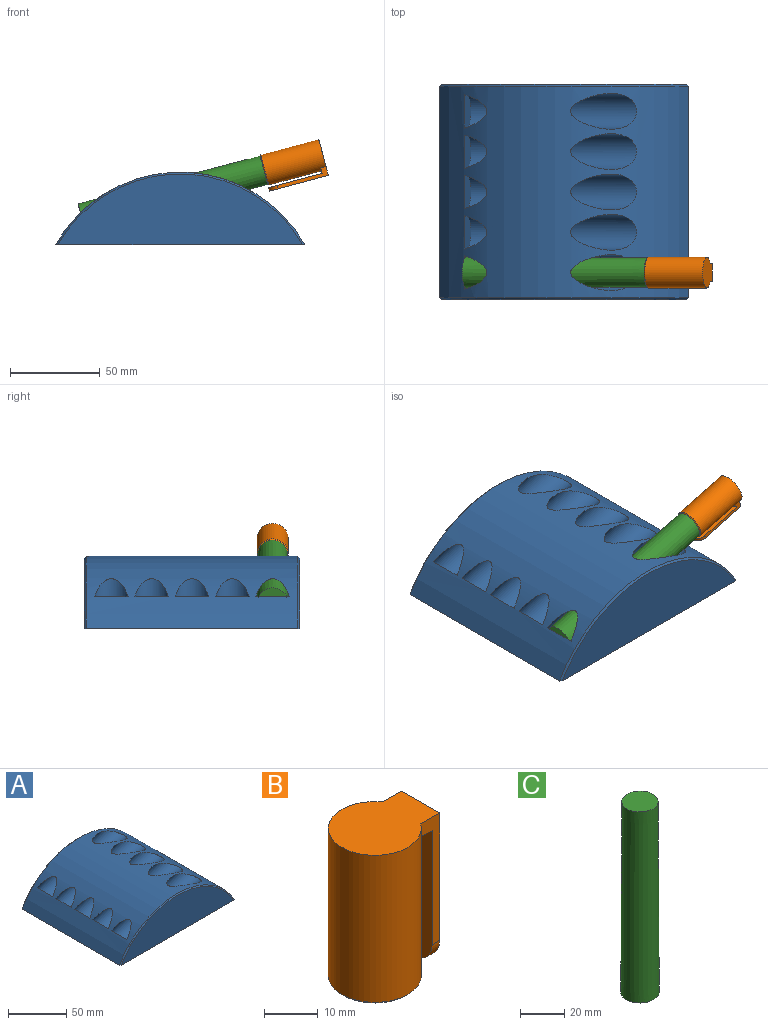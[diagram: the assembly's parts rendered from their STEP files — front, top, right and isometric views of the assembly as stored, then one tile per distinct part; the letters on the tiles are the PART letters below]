
ASSEMBLY  parts=3 mates=2
PART A: 30 faces, bbox 139x120x49.3 mm
  f0: plane 139x120mm, normal (0,0,-1), area 16514.7mm2, adj f1,f2,f3,f14,f15,f16,f17,f18
  f1: cylinder r=80mm len=139mm, axis (0,1,0), area 15845.9mm2, adj f0,f4,f5,f6,f7,f8,f9,f10
  f2: plane 136.69x39.38mm, normal (0,-1,0), area 3816.7mm2, adj f0,f14
  f3: plane 136.69x39.38mm, normal (0,1,0), area 3816.7mm2, adj f0,f15
  f4: cylinder r=10mm len=97.67mm, axis (-0.97,0,-0.26), area 4916.6mm2, adj f1,f5
  f5: plane 20x13.19mm, normal (0.97,0,0.26), area 228.6mm2, adj f1,f4
  f6: cylinder r=10mm len=97.67mm, axis (-0.97,0,-0.26), area 4916.6mm2, adj f1,f7
  f7: plane 20x13.19mm, normal (0.97,0,0.26), area 228.6mm2, adj f1,f6
  f8: cylinder r=10mm len=97.67mm, axis (-0.97,0,-0.26), area 4916.6mm2, adj f1,f9
  f9: plane 20x13.19mm, normal (0.97,0,0.26), area 228.6mm2, adj f1,f8
  f10: cylinder r=10mm len=97.67mm, axis (-0.97,0,-0.26), area 4916.6mm2, adj f1,f11
  f11: plane 20x13.19mm, normal (0.97,0,0.26), area 228.6mm2, adj f1,f10
  f12: cylinder r=10mm len=97.67mm, axis (-0.97,0,-0.26), area 4916.6mm2, adj f1,f13
  f13: plane 20x13.19mm, normal (0.97,0,0.26), area 228.6mm2, adj f1,f12
  f14: cone r=79mm half-angle=45deg, axis (0,1,0), area 235.9mm2, adj f0,f1,f2
  f15: cone r=80mm half-angle=45deg, axis (0,-1,0), area 235.9mm2, adj f0,f1,f3
  f16: plane 4.88x1mm, normal (0,-1,0), area 4.9mm2, adj f0,f17,f19,f24
  f17: cylinder r=2.5mm len=5mm, axis (0,0,-1), area 7.9mm2, adj f0,f16,f18,f24
  f18: plane 4.88x1mm, normal (0,1,0), area 4.9mm2, adj f0,f17,f19,f24
  f19: cylinder r=4mm len=8mm, axis (0,0,-1), area 19.7mm2, adj f0,f16,f18,f24
  f20: plane 4.88x1mm, normal (0,-1,0), area 4.9mm2, adj f0,f21,f23,f27
  f21: cylinder r=2.5mm len=5mm, axis (0,0,-1), area 7.9mm2, adj f0,f20,f22,f27
  f22: plane 4.88x1mm, normal (0,1,0), area 4.9mm2, adj f0,f21,f23,f27
  f23: cylinder r=4mm len=8mm, axis (0,0,-1), area 19.7mm2, adj f0,f20,f22,f27
  f24: plane 20x20mm, normal (0,0,1), area 232.7mm2, adj f16,f17,f18,f19,f25
  f25: cylinder r=10mm len=20mm, axis (0,0,-1), area 754mm2, adj f24,f26
  f26: plane 20x20mm, normal (0,0,-1), area 314.2mm2, adj f25
  f27: plane 20x20mm, normal (0,0,1), area 232.7mm2, adj f20,f21,f22,f23,f28
  f28: cylinder r=10mm len=20mm, axis (0,0,-1), area 754mm2, adj f27,f29
  f29: plane 20x20mm, normal (0,0,-1), area 314.2mm2, adj f28
PART B: 10 faces, bbox 20.7x17.3x34 mm
  f0: plane 10x3mm, normal (0,0,-1), area 19.2mm2, adj f1,f4,f5,f7
  f1: cylinder r=8.65mm len=33.5mm, axis (0,0,-1), area 1788.7mm2, adj f0,f2,f4,f5,f9
  f2: plane 20.71x17.3mm, normal (0,0,1), area 274.2mm2, adj f1,f4,f5,f6
  f3: plane 16.3x16.3mm, normal (0,0,-1), area 208.7mm2, adj f9
  f4: plane 29x5mm, normal (0,1,0), area 67mm2, adj f0,f1,f2,f6,f7,f8
  f5: plane 29x5mm, normal (0,-1,0), area 67mm2, adj f0,f1,f2,f6,f7,f8
  f6: plane 34x10mm, normal (1,0,0), area 329.3mm2, adj f2,f4,f5,f8
  f7: plane 31x10mm, normal (-1,0,0), area 299.3mm2, adj f0,f4,f5,f8
  f8: cylinder r=5mm len=10mm, axis (1,0,0), area 31.4mm2, adj f4,f5,f6,f7
  f9: cone r=8.65mm half-angle=45deg, axis (0,0,1), area 37.3mm2, adj f1,f3
PART C: 3 faces, bbox 17.3x17.3x105 mm
  f0: cone r=8.65mm half-angle=0.2deg, axis (0,0,-1), area 5555.6mm2, adj f1,f2
  f1: plane 16.38x16.38mm, normal (0,0,1), area 210.8mm2, adj f0
  f2: plane 17.3x17.3mm, normal (0,0,-1), area 235.1mm2, adj f0
PLACE A at identity fixed
PLACE B rot(axis=(0,1,0),75deg) t=(14.8,-105,14.32)mm
PLACE C rot(axis=(0,1,0),75deg) t=(14.8,-105,14.32)mm
MATE slider C.f0 <-> A.f4  axis (-0.97,0,-0.26) through (14.8,-105,14.32)mm
MATE fastened C.f0 <-> B.f1  axis (0.97,0,0.26) through (116.22,-105,41.49)mm
